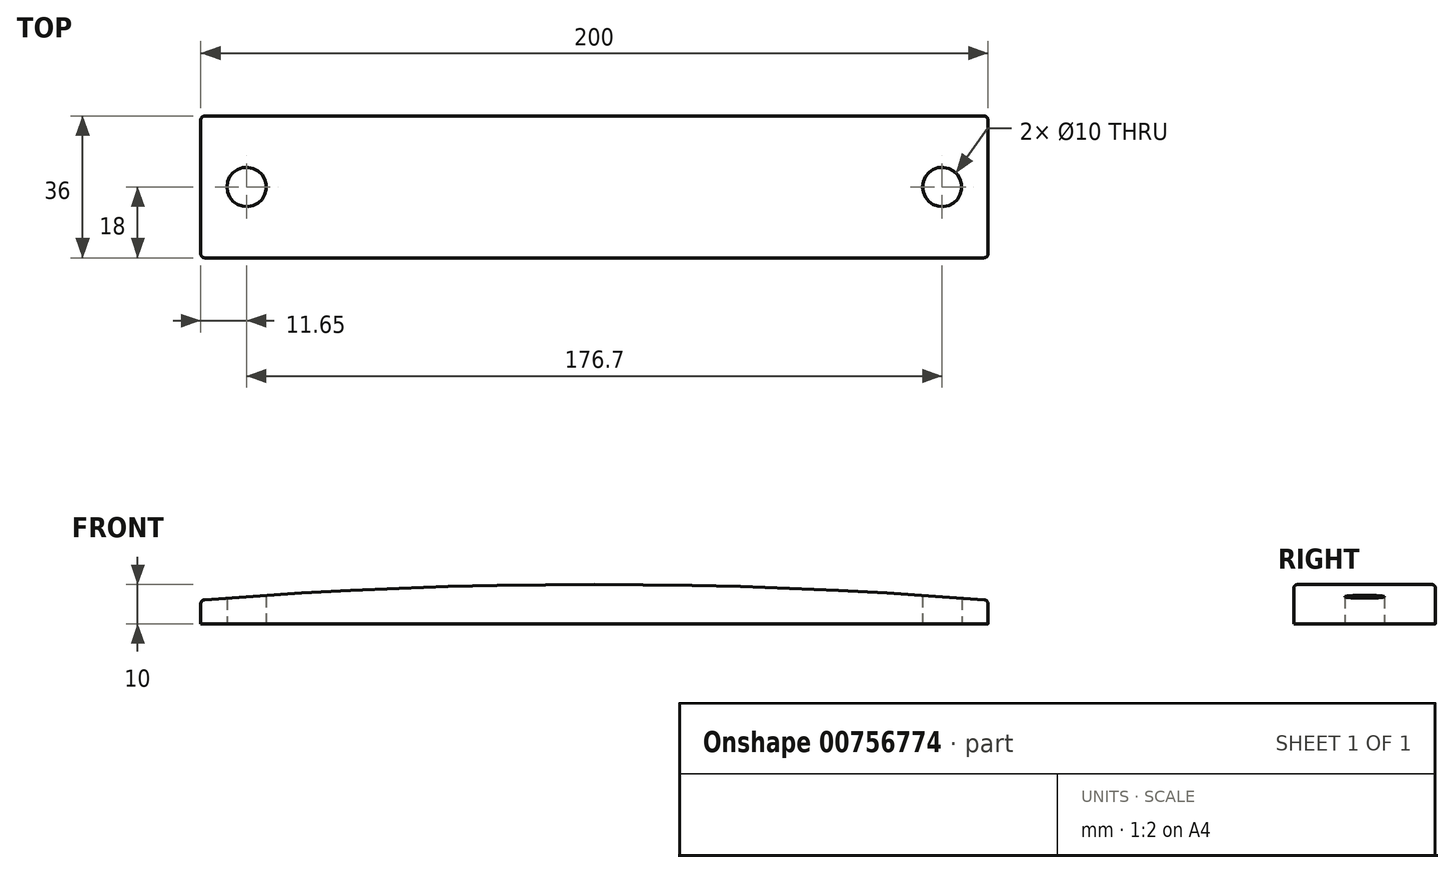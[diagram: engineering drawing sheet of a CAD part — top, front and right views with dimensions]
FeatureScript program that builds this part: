
annotation { "Feature Type Name" : "Feature", "Feature Type Description" : "" }
export const myFeature = defineFeature(function(context is Context, id is Id, definition is map)
    precondition{}
    {
        {
            var Q0;
            Q0=qCreatedBy(makeId("Front.planeOp"),FACE);
            var sketch = newSketch(context, id + "F0", { "sketchPlane" : qUnion([Q0])});
            skLineSegment(sketch, "E0", {"start": v(-100, 0) * mm, "end": v(100, 0) * mm});
            skLineSegment(sketch, "E1", {"start": v(100, 0) * mm, "end": v(100, 6) * mm});
            skLineSegment(sketch, "E2", {"start": v(-100, 0) * mm, "end": v(-100, 6) * mm});
            skLineSegment(sketch, "E3", {"start": v(-65.17, 10) * mm, "end": v(0, 10) * mm, "construction": true});
            skArc(sketch, "E4", {"start": v(100, 6) * mm, "mid": v(0, 10) * mm, "end": v(-100, 6) * mm});
            skSolve(sketch);
        }
        {
            var Q0;
            Q0=makeQuery(id+"F0.imprint","IMPRINT",FACE,{"disambiguationData":[TD([[makeQuery(id+"F0.imprint","IMPRINT",EDGE,{"derivedFrom":sQuery(id+"F0.wireOp",EDGE,"E0")}),1.0]])]});
            extrude(context, id + "F1", {"entities" : qUnion([Q0]), "depth" : 18 * mm, "offsetDistance" : 25 * mm, "hasSecondDirection" : true, "secondDirectionOppositeDirection" : true, "secondDirectionDepth" : 18 * mm});
        }
        {
            var Q0;
            Q0=qCreatedBy(makeId("Top.planeOp"),FACE);
            var sketch = newSketch(context, id + "F2", { "sketchPlane" : qUnion([Q0])});
            skCircle(sketch, "E5", {"center": v(-88.35, 0) * mm, "radius": 5 * mm});
            skCircle(sketch, "E6", {"center": v(88.35, 0) * mm, "radius": 5 * mm});
            skSolve(sketch);
        }
        {
            var Q0;
            Q0 = qSketchRegion(id + "F2", true);
            extrude(context, id + "F3", {"entities" : qUnion([Q0]), "operationType" : NewBodyOperationType.REMOVE, "depth" : 25 * mm, "offsetDistance" : 25 * mm});
        }
        {
            var Q0;
            Q0=makeQuery(id+"F1.opExtrude","SWEPT_EDGE",EDGE,{"disambiguationData":[OSD([sQuery(id+"F0.wireOp",EDGE,"E2"),sQuery(id+"F0.wireOp",EDGE,"E4")])]});
            var Q1;
            Q1=makeQuery(id+"F1.opExtrude","CAP_EDGE",EDGE,{"disambiguationData":[OSD([sQuery(id+"F0.wireOp",EDGE,"E4")])],"isStart":false});
            var Q2;
            Q2=makeQuery(id+"F1.opExtrude","SWEPT_EDGE",EDGE,{"disambiguationData":[OSD([sQuery(id+"F0.wireOp",EDGE,"E1"),sQuery(id+"F0.wireOp",EDGE,"E4")])]});
            var Q3;
            Q3=makeQuery(id+"F1.opExtrude","CAP_EDGE",EDGE,{"disambiguationData":[OSD([sQuery(id+"F0.wireOp",EDGE,"E4")])],"isStart":true});
            var Q4;
            Q4=makeQuery(id+"F1.opExtrude","CAP_EDGE",EDGE,{"disambiguationData":[OSD([sQuery(id+"F0.wireOp",EDGE,"E1")])],"isStart":false});
            var Q5;
            Q5=makeQuery(id+"F1.opExtrude","CAP_EDGE",EDGE,{"disambiguationData":[OSD([sQuery(id+"F0.wireOp",EDGE,"E1")])],"isStart":true});
            var Q6;
            Q6=makeQuery(id+"F1.opExtrude","CAP_EDGE",EDGE,{"disambiguationData":[OSD([sQuery(id+"F0.wireOp",EDGE,"E2")])],"isStart":true});
            var Q7;
            Q7=makeQuery(id+"F1.opExtrude","CAP_EDGE",EDGE,{"disambiguationData":[OSD([sQuery(id+"F0.wireOp",EDGE,"E2")])],"isStart":false});
            fillet(context, id + "F4", {"entities" : qUnion([Q0, Q1, Q2, Q3, Q4, Q5, Q6, Q7]), "radius" : 1 * mm, "tangentPropagation" : true, "allowEdgeOverflow" : false});
        }
    });
